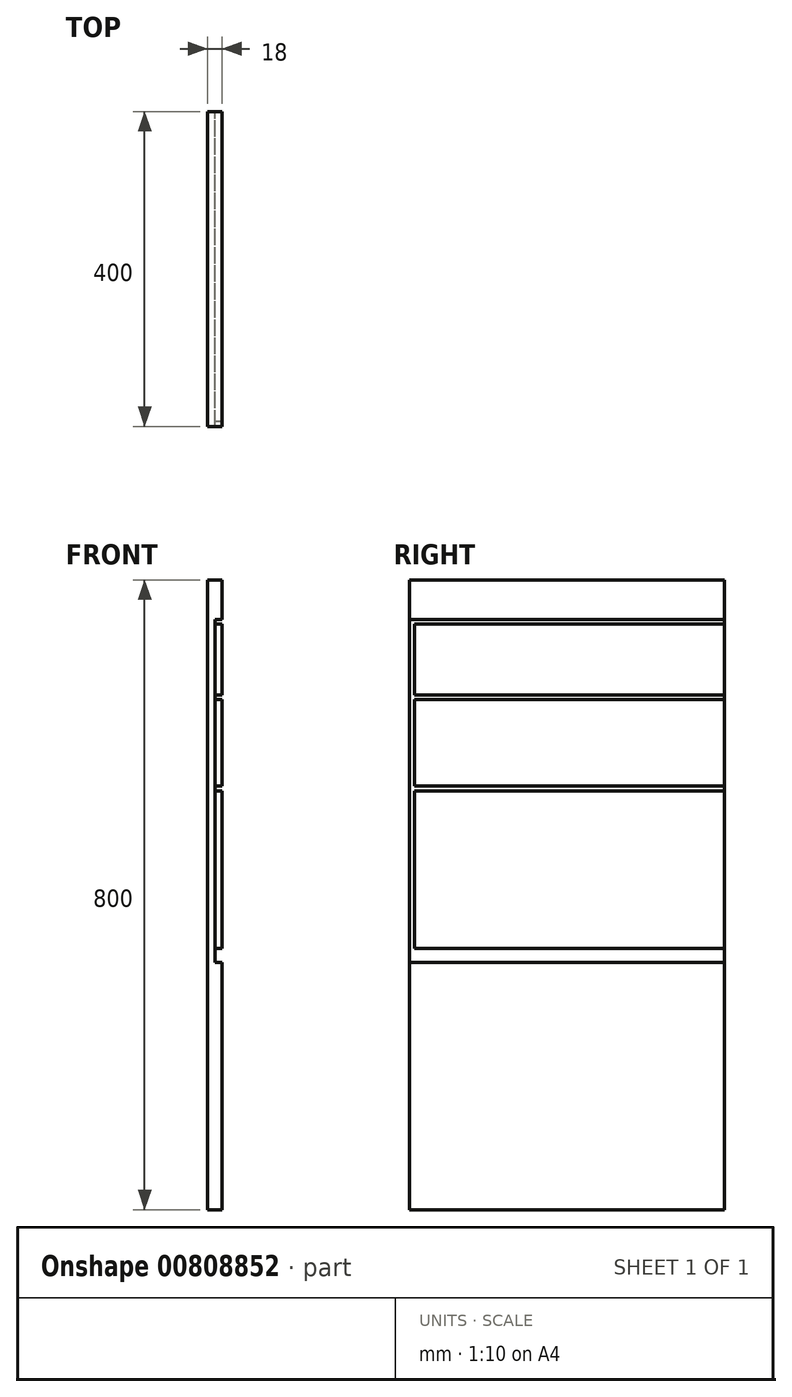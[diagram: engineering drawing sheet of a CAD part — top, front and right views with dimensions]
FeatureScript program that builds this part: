
annotation { "Feature Type Name" : "Feature", "Feature Type Description" : "" }
export const myFeature = defineFeature(function(context is Context, id is Id, definition is map)
    precondition{}
    {
        {
            var Q0;
            Q0=qCreatedBy(makeId("Right.planeOp"),FACE);
            var sketch = newSketch(context, id + "F0", { "sketchPlane" : qUnion([Q0])});
            skLineSegment(sketch, "E0.bottom", {"start": v(0, 0) * mm, "end": v(400, 0) * mm});
            skLineSegment(sketch, "E0.top", {"start": v(0, 800) * mm, "end": v(400, 800) * mm});
            skLineSegment(sketch, "E0.left", {"start": v(0, 0) * mm, "end": v(0, 800) * mm});
            skLineSegment(sketch, "E0.right", {"start": v(400, 0) * mm, "end": v(400, 800) * mm});
            skLineSegment(sketch, "E1.top", {"start": v(400, 0) * mm, "end": v(394, 0) * mm});
            skLineSegment(sketch, "E1.left", {"start": v(400, 800) * mm, "end": v(400, 0) * mm});
            skLineSegment(sketch, "E2", {"start": v(0, 800) * mm, "end": v(0, 750) * mm});
            skLineSegment(sketch, "E3.bottom", {"start": v(0, 750) * mm, "end": v(400, 750) * mm});
            skLineSegment(sketch, "E3.top", {"start": v(0, 744) * mm, "end": v(400, 744) * mm});
            skLineSegment(sketch, "E3.left", {"start": v(0, 750) * mm, "end": v(0, 744) * mm});
            skLineSegment(sketch, "E3.right", {"start": v(400, 750) * mm, "end": v(400, 744) * mm});
            skLineSegment(sketch, "E4", {"start": v(0, 744) * mm, "end": v(0, 654) * mm});
            skLineSegment(sketch, "E5.bottom", {"start": v(0, 654) * mm, "end": v(400, 654) * mm});
            skLineSegment(sketch, "E5.top", {"start": v(0, 648) * mm, "end": v(400, 648) * mm});
            skLineSegment(sketch, "E5.left", {"start": v(0, 654) * mm, "end": v(0, 648) * mm});
            skLineSegment(sketch, "E5.right", {"start": v(400, 654) * mm, "end": v(400, 648) * mm});
            skLineSegment(sketch, "E6", {"start": v(0, 648) * mm, "end": v(0, 538) * mm});
            skLineSegment(sketch, "E7.bottom", {"start": v(0, 538) * mm, "end": v(400, 538) * mm});
            skLineSegment(sketch, "E7.top", {"start": v(0, 532) * mm, "end": v(400, 532) * mm});
            skLineSegment(sketch, "E7.left", {"start": v(0, 538) * mm, "end": v(0, 532) * mm});
            skLineSegment(sketch, "E7.right", {"start": v(400, 538) * mm, "end": v(400, 532) * mm});
            skLineSegment(sketch, "E8", {"start": v(0, 532) * mm, "end": v(0, 332) * mm});
            skLineSegment(sketch, "E9.bottom", {"start": v(0, 332) * mm, "end": v(400, 332) * mm});
            skLineSegment(sketch, "E9.top", {"start": v(0, 314) * mm, "end": v(400, 314) * mm});
            skLineSegment(sketch, "E9.left", {"start": v(0, 332) * mm, "end": v(0, 314) * mm});
            skLineSegment(sketch, "E9.right", {"start": v(400, 332) * mm, "end": v(400, 314) * mm});
            skLineSegment(sketch, "E10.bottom", {"start": v(0, 800) * mm, "end": v(6, 800) * mm});
            skLineSegment(sketch, "E10.top", {"start": v(0, 0) * mm, "end": v(6, 0) * mm});
            skLineSegment(sketch, "E10.left", {"start": v(0, 800) * mm, "end": v(0, 0) * mm});
            skLineSegment(sketch, "E10.right", {"start": v(6, 800) * mm, "end": v(6, 0) * mm});
            skSolve(sketch);
        }
        {
            var Q0;
            {var subQ0=sQuery(id+"F0.wireOp",EDGE,"E0.top");Q0=makeQuery(id+"F0.imprint","IMPRINT",FACE,{"disambiguationData":[TD([[makeQuery(id+"F0.imprint","IMPRINT",EDGE,{"derivedFrom":subQ0}),-1.0]])]});}
            var Q1;
            {var subQ0=sQuery(id+"F0.wireOp",EDGE,"E3.top");var subQ5=sQuery(id+"F0.wireOp",EDGE,"E10.right");var subQ7=makeQuery(id+"F0.imprint","INTERSECT",VERTEX,{"derivedFrom":[subQ0,subQ5]});Q1=makeQuery(id+"F0.imprint","IMPRINT",FACE,{"disambiguationData":[TD([[makeQuery(id+"F0.imprint","IMPRINT",EDGE,{"disambiguationData":[TD([[subQ7,-1.0]])],"derivedFrom":subQ5}),1.0]])]});}
            var Q2;
            {var subQ0=sQuery(id+"F0.wireOp",EDGE,"E5.top");var subQ5=sQuery(id+"F0.wireOp",EDGE,"E10.right");var subQ6=makeQuery(id+"F0.imprint","INTERSECT",VERTEX,{"derivedFrom":[subQ0,subQ5]});Q2=makeQuery(id+"F0.imprint","IMPRINT",FACE,{"disambiguationData":[TD([[makeQuery(id+"F0.imprint","IMPRINT",EDGE,{"disambiguationData":[TD([[subQ6,-1.0]])],"derivedFrom":subQ5}),1.0]])]});}
            var Q3;
            {var subQ0=sQuery(id+"F0.wireOp",EDGE,"E7.top");var subQ5=sQuery(id+"F0.wireOp",EDGE,"E10.right");var subQ6=makeQuery(id+"F0.imprint","INTERSECT",VERTEX,{"derivedFrom":[subQ0,subQ5]});Q3=makeQuery(id+"F0.imprint","IMPRINT",FACE,{"disambiguationData":[TD([[makeQuery(id+"F0.imprint","IMPRINT",EDGE,{"disambiguationData":[TD([[subQ6,-1.0]])],"derivedFrom":subQ5}),1.0]])]});}
            var Q4;
            {var subQ6=sQuery(id+"F0.wireOp",EDGE,"E0.bottom");Q4=makeQuery(id+"F0.imprint","IMPRINT",FACE,{"disambiguationData":[TD([[makeQuery(id+"F0.imprint","IMPRINT",EDGE,{"derivedFrom":subQ6}),1.0]])]});}
            extrude(context, id + "F1", {"entities" : qUnion([Q0, Q1, Q2, Q3, Q4]), "depth" : 18 * mm, "offsetDistance" : 25 * mm});
        }
        {
            var Q0;
            {var subQ5=sQuery(id+"F0.wireOp",EDGE,"E10.top");Q0=makeQuery(id+"F0.imprint","IMPRINT",FACE,{"disambiguationData":[TD([[makeQuery(id+"F0.imprint","IMPRINT",EDGE,{"derivedFrom":subQ5}),1.0]])]});}
            var Q1;
            {var subQ0=sQuery(id+"F0.wireOp",EDGE,"E10.left");var subQ1=sQuery(id+"F0.wireOp",EDGE,"E9.bottom");var subQ2=makeQuery(id+"F0.imprint","INTERSECT",VERTEX,{"derivedFrom":[subQ1,subQ0]});Q1=makeQuery(id+"F0.imprint","IMPRINT",FACE,{"disambiguationData":[TD([[makeQuery(id+"F0.imprint","IMPRINT",EDGE,{"disambiguationData":[TD([[subQ2,-1.0]])],"derivedFrom":subQ1}),-1.0]])]});}
            var Q2;
            {var subQ0=sQuery(id+"F0.wireOp",EDGE,"E9.right");Q2=makeQuery(id+"F0.imprint","IMPRINT",FACE,{"disambiguationData":[TD([[makeQuery(id+"F0.imprint","IMPRINT",EDGE,{"derivedFrom":subQ0}),-1.0]])]});}
            var Q3;
            {var subQ0=sQuery(id+"F0.wireOp",EDGE,"E10.left");var subQ1=sQuery(id+"F0.wireOp",EDGE,"E7.top");var subQ2=makeQuery(id+"F0.imprint","INTERSECT",VERTEX,{"derivedFrom":[subQ1,subQ0]});Q3=makeQuery(id+"F0.imprint","IMPRINT",FACE,{"disambiguationData":[TD([[makeQuery(id+"F0.imprint","IMPRINT",EDGE,{"disambiguationData":[TD([[subQ2,-1.0]])],"derivedFrom":subQ1}),-1.0]])]});}
            var Q4;
            {var subQ0=sQuery(id+"F0.wireOp",EDGE,"E7.right");Q4=makeQuery(id+"F0.imprint","IMPRINT",FACE,{"disambiguationData":[TD([[makeQuery(id+"F0.imprint","IMPRINT",EDGE,{"derivedFrom":subQ0}),-1.0]])]});}
            var Q5;
            {var subQ0=sQuery(id+"F0.wireOp",EDGE,"E5.right");Q5=makeQuery(id+"F0.imprint","IMPRINT",FACE,{"disambiguationData":[TD([[makeQuery(id+"F0.imprint","IMPRINT",EDGE,{"derivedFrom":subQ0}),-1.0]])]});}
            var Q6;
            {var subQ0=sQuery(id+"F0.wireOp",EDGE,"E10.left");var subQ1=sQuery(id+"F0.wireOp",EDGE,"E5.top");var subQ2=makeQuery(id+"F0.imprint","INTERSECT",VERTEX,{"derivedFrom":[subQ1,subQ0]});Q6=makeQuery(id+"F0.imprint","IMPRINT",FACE,{"disambiguationData":[TD([[makeQuery(id+"F0.imprint","IMPRINT",EDGE,{"disambiguationData":[TD([[subQ2,-1.0]])],"derivedFrom":subQ1}),-1.0]])]});}
            var Q7;
            {var subQ0=sQuery(id+"F0.wireOp",EDGE,"E10.left");var subQ1=sQuery(id+"F0.wireOp",EDGE,"E5.bottom");var subQ2=makeQuery(id+"F0.imprint","INTERSECT",VERTEX,{"derivedFrom":[subQ1,subQ0]});Q7=makeQuery(id+"F0.imprint","IMPRINT",FACE,{"disambiguationData":[TD([[makeQuery(id+"F0.imprint","IMPRINT",EDGE,{"disambiguationData":[TD([[subQ2,-1.0]])],"derivedFrom":subQ1}),-1.0]])]});}
            var Q8;
            {var subQ5=sQuery(id+"F0.wireOp",EDGE,"E10.bottom");Q8=makeQuery(id+"F0.imprint","IMPRINT",FACE,{"disambiguationData":[TD([[makeQuery(id+"F0.imprint","IMPRINT",EDGE,{"derivedFrom":subQ5}),-1.0]])]});}
            var Q9;
            {var subQ0=sQuery(id+"F0.wireOp",EDGE,"E10.left");var subQ1=sQuery(id+"F0.wireOp",EDGE,"E3.bottom");var subQ2=makeQuery(id+"F0.imprint","INTERSECT",VERTEX,{"derivedFrom":[subQ1,subQ0]});Q9=makeQuery(id+"F0.imprint","IMPRINT",FACE,{"disambiguationData":[TD([[makeQuery(id+"F0.imprint","IMPRINT",EDGE,{"disambiguationData":[TD([[subQ2,-1.0]])],"derivedFrom":subQ1}),-1.0]])]});}
            var Q10;
            {var subQ0=sQuery(id+"F0.wireOp",EDGE,"E10.left");var subQ1=sQuery(id+"F0.wireOp",EDGE,"E3.top");var subQ2=makeQuery(id+"F0.imprint","INTERSECT",VERTEX,{"derivedFrom":[subQ1,subQ0]});Q10=makeQuery(id+"F0.imprint","IMPRINT",FACE,{"disambiguationData":[TD([[makeQuery(id+"F0.imprint","IMPRINT",EDGE,{"disambiguationData":[TD([[subQ2,-1.0]])],"derivedFrom":subQ1}),-1.0]])]});}
            var Q11;
            {var subQ0=sQuery(id+"F0.wireOp",EDGE,"E3.right");Q11=makeQuery(id+"F0.imprint","IMPRINT",FACE,{"disambiguationData":[TD([[makeQuery(id+"F0.imprint","IMPRINT",EDGE,{"derivedFrom":subQ0}),-1.0]])]});}
            var Q12;
            {var subQ0=sQuery(id+"F0.wireOp",EDGE,"E10.left");var subQ1=sQuery(id+"F0.wireOp",EDGE,"E7.bottom");var subQ2=makeQuery(id+"F0.imprint","INTERSECT",VERTEX,{"derivedFrom":[subQ1,subQ0]});Q12=makeQuery(id+"F0.imprint","IMPRINT",FACE,{"disambiguationData":[TD([[makeQuery(id+"F0.imprint","IMPRINT",EDGE,{"disambiguationData":[TD([[subQ2,-1.0]])],"derivedFrom":subQ1}),-1.0]])]});}
            extrude(context, id + "F2", {"entities" : qUnion([Q0, Q1, Q2, Q3, Q4, Q5, Q6, Q7, Q8, Q9, Q10, Q11, Q12]), "operationType" : NewBodyOperationType.ADD, "depth" : 9 * mm, "offsetDistance" : 25 * mm});
        }
    });
